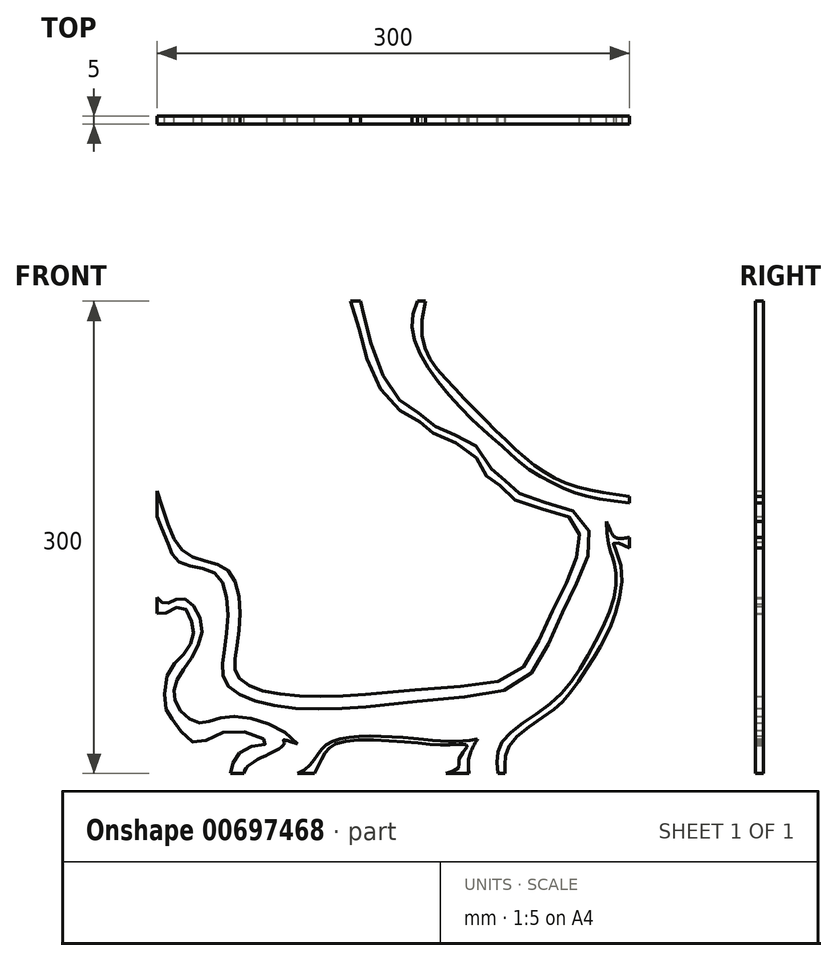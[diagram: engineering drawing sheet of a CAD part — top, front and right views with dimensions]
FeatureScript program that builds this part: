
annotation { "Feature Type Name" : "Feature", "Feature Type Description" : "" }
export const myFeature = defineFeature(function(context is Context, id is Id, definition is map)
    precondition{}
    {
        {
            var Q0;
            Q0=qCreatedBy(makeId("Front.planeOp"),FACE);
            var sketch = newSketch(context, id + "F0", { "sketchPlane" : qUnion([Q0])});
            skLineSegment(sketch, "E0.bottom", {"start": v(-27.2, 150) * mm, "end": v(-20.7, 150) * mm});
            skLineSegment(sketch, "E0.top", {"start": v(-103.36, -150) * mm, "end": v(-94.81, -150) * mm});
            skLineSegment(sketch, "E0.left", {"start": v(-150, 29.4) * mm, "end": v(-150, 13.31) * mm});
            skLineSegment(sketch, "E0.right", {"start": v(150, 25.92) * mm, "end": v(150, 21.84) * mm});
            skPoint(sketch, "E0.middle", {"position": v(0, 0) * mm});
            skFitSpline(sketch, "E1", {"points": [v(20.42, 150) * mm, v(32.17, 101.95) * mm, v(71.71, 61.39) * mm, v(105.12, 36.44) * mm, v(150, 25.92) * mm], "startDerivative": vector(-77.75, -307.2) * mm, "endDerivative": vector(194.48, -23.45) * mm});
            skFitSpline(sketch, "E2", {"points": [v(-27.2, 150) * mm, v(-18.1, 117.5) * mm, v(0, 83.97) * mm, v(17.71, 72.64) * mm, v(26.84, 65.16) * mm, v(49.75, 53.95) * mm, v(58.87, 39.42) * mm, v(67.03, 33.56) * mm, v(80.11, 21.9) * mm, v(111.1, 13.21) * mm, v(118.26, 0) * mm, v(112.8, -22.98) * mm, v(96.75, -55.85) * mm, v(78.57, -86.03) * mm, v(29.1, -95.65) * mm, v(-59.57, -100.78) * mm, v(-98.86, -88.31) * mm, v(-98.21, -62.08) * mm, v(-104.98, -21.14) * mm, v(-131.44, -10.44) * mm, v(-150, 29.4) * mm], "startDerivative": vector(276.19, -544.8) * mm, "endDerivative": vector(-273.28, 796.72) * mm});
            skPoint(sketch, "E3.1.internal.snap0", {"position": v(150, 0) * mm});
            skFitSpline(sketch, "E3", {"points": [v(135.25, 10.1) * mm, v(140.76, 0) * mm, v(150, 0) * mm], "startDerivative": vector(13.5, -23.95) * mm, "endDerivative": vector(21.86, 4.33) * mm});
            skFitSpline(sketch, "E4", {"points": [v(135.25, 10.1) * mm, v(137.62, -8.24) * mm, v(139.94, -14.92) * mm, v(141.08, -33.68) * mm, v(125.16, -72.33) * mm, v(100.15, -105.3) * mm, v(68.89, -130.31) * mm, v(66.62, -150) * mm], "startDerivative": vector(5.78, -169.03) * mm, "endDerivative": vector(18.76, -161.26) * mm});
            skFitSpline(sketch, "E5", {"points": [v(53.54, -128.22) * mm, v(47.98, -140.52) * mm, v(48.04, -150) * mm], "startDerivative": vector(-11.5, -16.78) * mm, "endDerivative": vector(1.07, -21.46) * mm});
            skFitSpline(sketch, "E6", {"points": [v(53.54, -128.22) * mm, v(16.7, -128.22) * mm, v(-41.53, -131.26) * mm, v(-60.7, -150) * mm], "startDerivative": vector(-109.66, -22.19) * mm, "endDerivative": vector(-117.79, -44.9) * mm});
            skFitSpline(sketch, "E7", {"points": [v(-60.7, -131.26) * mm, v(-69.22, -131.26) * mm, v(-94.81, -150) * mm], "startDerivative": vector(-116.44, 38.62) * mm, "endDerivative": vector(-2.41, -37.38) * mm});
            skFitSpline(sketch, "E8", {"points": [v(-60.7, -131.26) * mm, v(-103.9, -113.83) * mm, v(-124.37, -117.8) * mm, v(-138.58, -103.6) * mm, v(-134.6, -85.97) * mm, v(-121.53, -58.7) * mm, v(-133.47, -38.8) * mm, v(-144.27, -42.2) * mm, v(-150, -38.23) * mm], "startDerivative": vector(-150.66, 182.8) * mm, "endDerivative": vector(-68.9, 82.85) * mm});
            skFitSpline(sketch, "E9", {"points": [v(-20.7, 150) * mm, v(-19.28, 142.27) * mm, v(-11.6, 114.7) * mm, v(5.16, 86.28) * mm, v(19.65, 76.62) * mm, v(32.44, 66.67) * mm, v(49.75, 60.71) * mm, v(64.62, 40.43) * mm, v(72.05, 35.36) * mm, v(83.88, 25.56) * mm, v(112.6, 17.45) * mm, v(125.16, 0) * mm, v(118.26, -25.15) * mm, v(102.43, -58.7) * mm, v(81.96, -91.66) * mm, v(28.53, -103.03) * mm, v(-60.7, -108.71) * mm, v(-106.18, -92.8) * mm, v(-106.18, -63.8) * mm, v(-111.87, -24.02) * mm, v(-135.17, -16.06) * mm, v(-144.48, -0.56) * mm, v(-150, 13.31) * mm], "startDerivative": vector(-9.16, -545.06) * mm, "endDerivative": vector(-135.7, 442.01) * mm});
            skFitSpline(sketch, "E10", {"points": [v(15.27, 150) * mm, v(12.9, 127.63) * mm, v(28.11, 99.24) * mm, v(53.46, 71.53) * mm, v(70.02, 57) * mm, v(84.22, 44.49) * mm, v(103.48, 33.34) * mm, v(121.74, 26.24) * mm, v(150, 21.84) * mm], "startDerivative": vector(-84.35, -185.7) * mm, "endDerivative": vector(227, -25.8) * mm});
            skFitSpline(sketch, "E11", {"points": [v(150, -6.88) * mm, v(139.94, -3.5) * mm, v(144.04, -14.92) * mm, v(142.01, -45.41) * mm, v(134.58, -63.67) * mm, v(125.16, -79.89) * mm, v(111.26, -100.17) * mm, v(99.1, -111.66) * mm, v(76.1, -128.9) * mm, v(71.04, -141.06) * mm, v(71.04, -150) * mm], "startDerivative": vector(-177.67, 83.92) * mm, "endDerivative": vector(5.55, -121.92) * mm});
            skFitSpline(sketch, "E12", {"points": [v(-49.94, -150) * mm, v(-43.88, -138.02) * mm, v(-34.75, -130.59) * mm, v(10.88, -130.25) * mm, v(38.25, -131.94) * mm, v(47.1, -132.18) * mm, v(41.8, -140.52) * mm, v(41.8, -145.9) * mm, v(33.52, -150) * mm], "startDerivative": vector(44.58, 106.73) * mm, "endDerivative": vector(-111.9, -37.47) * mm});
            skFitSpline(sketch, "E13", {"points": [v(-150, -48.46) * mm, v(-143.58, -47.78) * mm, v(-133.78, -44.06) * mm, v(-128.03, -54.2) * mm, v(-127.36, -63.8) * mm, v(-133.44, -74.82) * mm, v(-142.57, -85.3) * mm, v(-144.6, -107.94) * mm, v(-138.85, -117.4) * mm, v(-125.67, -130.6) * mm, v(-103.02, -122.81) * mm, v(-80.04, -130.6) * mm, v(-90.52, -132.95) * mm, v(-100.66, -141.06) * mm, v(-103.36, -150) * mm], "startDerivative": vector(120.5, -10.2) * mm, "endDerivative": vector(-27.5, -158.3) * mm});
            skLineSegment(sketch, "E14.trimOffspring", {"start": v(-150, -38.23) * mm, "end": v(-150, -48.46) * mm});
            skLineSegment(sketch, "E15.trimOffspring", {"start": v(-60.7, -150) * mm, "end": v(-49.94, -150) * mm});
            skLineSegment(sketch, "E16.trimOffspring", {"start": v(33.52, -150) * mm, "end": v(48.04, -150) * mm});
            skLineSegment(sketch, "E17.trimOffspring", {"start": v(15.27, 150) * mm, "end": v(20.42, 150) * mm});
            skLineSegment(sketch, "E18.trimOffspring", {"start": v(66.62, -150) * mm, "end": v(71.04, -150) * mm});
            skLineSegment(sketch, "E19.trimOffspring", {"start": v(150, 0) * mm, "end": v(150, -6.88) * mm});
            skLineSegment(sketch, "E20", {"start": v(-17.59, -99.7) * mm, "end": v(-17.2, -107.7) * mm});
            skLineSegment(sketch, "E21", {"start": v(-17.2, -107.7) * mm, "end": v(-17.59, -99.7) * mm});
            skSolve(sketch);
        }
        {
            var Q0;
            Q0=qSketchRegion(id+"F0",true);
            extrude(context, id + "F1", {"entities" : qUnion([Q0]), "depth" : 5 * mm, "offsetDistance" : 25 * mm});
        }
    });
